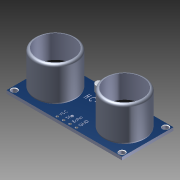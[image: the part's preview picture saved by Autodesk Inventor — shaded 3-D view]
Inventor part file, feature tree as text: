
AUTODESK INVENTOR PART (.ipt)
format: ipt  version: 2015 (Build 190159000, 159)  size: 978,944 bytes
history: native  units: in
note: dims shown in document units (in); Inventor stores cm internally (conversion verified against a paired STEP export)
features: other x12, imported_body x12, fillet x1
ambient origin geometry x8: Origin, YZ Plane, XZ Plane, XY Plane, X Axis, Y Axis, Z Axis, Center Point
bodies: Body1 (feature_tree), Body2 (feature_tree), Body3 (feature_tree), Body4 (feature_tree), Body5 (feature_tree), Body6 (feature_tree), Body7 (feature_tree), Body8 (feature_tree), Body9 (feature_tree), Body10 (feature_tree), Body11 (feature_tree), Body12 (feature_tree)
feature tree (25):
  fillet  "Fillet6"  [1 undecoded]
  other  "UltraSonic.ipt1"
  other  "Boss-Extrude4[1]"
  other  "Boss-Extrude4[2]"
  other  "Boss-Extrude4[3]"
  other  "Boss-Extrude4[4]"
  other  "Boss-Extrude4[5]"
  other  "Boss-Extrude4[6]"
  other  "Boss-Extrude4[7]"
  other  "Boss-Extrude9"
  other  "Cut-Extrude6[1]"
  other  "Cut-Extrude9"
  other  "Cut-Extrude10"
  imported_body  "Base1"
  imported_body  "Base2"
  imported_body  "Base3"
  imported_body  "Base4"
  imported_body  "Base5"
  imported_body  "Base6"
  imported_body  "Base7"
  imported_body  "Base8"
  imported_body  "Base9"
  imported_body  "Base10"
  imported_body  "Base11"
  imported_body  "Base12"
note: 1 required parameter value undecoded (feature->parameter linkage not recoverable at this tier; creation-order binding heuristic only, values carry confidence <= 0.55)
